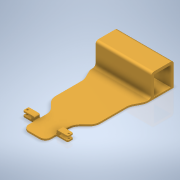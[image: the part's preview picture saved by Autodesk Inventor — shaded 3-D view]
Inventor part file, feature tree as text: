
AUTODESK INVENTOR PART (.ipt)
format: ipt  version: 2020 (Build 240168000, 168)  size: 318,464 bytes
history: native  units: mm
features: fillet x14, sketch x4, extrude x3, plane x2, hole x1, mirror x1
ambient origin geometry x8: Origin, YZ Plane, XZ Plane, XY Plane, X Axis, Y Axis, Z Axis, Center Point
bodies: Body1 (feature_tree)
feature tree (25):
  extrude  "Extrusion2"  Depth=60.0mm
  plane  "Work Plane1"
  extrude  "Extrusion3"  Depth=40.0mm
  fillet  "Fillet1"  Radius=50.0mm
  fillet  "Fillet2"  Radius=50.0mm
  fillet  "Fillet3"  Radius=20.0mm
  fillet  "Fillet4"  Radius=20.0mm
  fillet  "Fillet5"  Radius=40.0mm
  hole  "Hole1"  [1 undecoded]
  plane  "Work Plane2"
  mirror  "Mirror1"
  fillet  "Fillet6"  Radius=10.0mm
  fillet  "Fillet7"  Radius=20.0mm
  fillet  "Fillet8"  Radius=200.0mm
  fillet  "Fillet9"  Radius=20.0mm
  fillet  "Fillet10"  Radius=10.0mm
  fillet  "Fillet11"  Radius=3.0mm
  extrude  "Extrusion4"  Depth=5.0mm
  fillet  "Fillet12"  Radius=2.5mm
  fillet  "Fillet13"  Radius=2.5mm
  fillet  "Fillet14"  Radius=20.0mm
  sketch  "Sketch1"  dims[d23=50.0mm d24=60.0mm]
  sketch  "Sketch4"  dims[d25=60.0mm d26=50.0mm d27=50.0mm d28=50.0mm d29=20.0mm d30=20.0mm d31=40.0mm]
  sketch  "Sketch5"  dims[d32=100.0mm d34=10.0mm d35=10.0mm d36=20.0mm d37=200.0mm d38=20.0mm d39=10.0mm d40=3.0mm d41=0.0mm]
  sketch  "Sketch6"  dims[d42=-25.0mm d61=15.0mm d66=5.0mm d67=2.5mm d68=2.5mm d69=20.0mm d70=15.0mm d71=2.0mm d72=10.0mm d73=0.0mm d74=2.0mm d75=2.0mm d76=0.5mm d77=1.26mm d78=0.5mm d79=3.0mm d80=6.0mm d81=4.0mm d82=2.0mm d83=90.0deg d84=8.0mm d85=20.594885mm d86=3.0mm d87=5.0mm d88=50.0mm d89=2.0mm d90=2.12mm d91=1.0mm d92=2.46mm d93=1.0mm d94=2.0mm d95=40.0mm d96=40.0mm d97=5.0mm d98=5.0mm d100=5.0mm d101=100.0mm d102=0.0mm d103=5.0mm d104=5.0mm d105=5.0mm d57=0.5mm d58=0.872665mm d59=0.5mm d60=0.872665mm]
note: 1 required parameter value undecoded (feature->parameter linkage not recoverable at this tier; creation-order binding heuristic only, values carry confidence <= 0.55)
